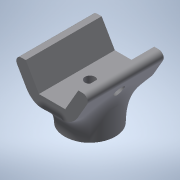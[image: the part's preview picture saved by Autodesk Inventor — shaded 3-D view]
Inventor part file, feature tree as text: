
AUTODESK INVENTOR PART (.ipt)
format: ipt  version: 2020 (Build 240168000, 168)  size: 770,560 bytes
history: native  units: mm
features: other x7, extrude x4, sketch x4, fillet x3, mirror x1, reference x1
ambient origin geometry x8: Origin, YZ Plane, XZ Plane, XY Plane, X Axis, Y Axis, Z Axis, Center Point
bodies: Body1 (feature_tree)
feature tree (20):
  other  "Твердое тело1"
  extrude  "Выдавливание1"  Depth=5.0mm
  other  "Непосредственное редактирование1"
  fillet  "Сопряжение1"  Radius=5.0mm
  extrude  "Выдавливание2"  Depth=5.0mm
  extrude  "Выдавливание3"  Depth=30.0mm TaperAngle=0.0deg
  fillet  "Сопряжение4"  [1 undecoded]
  fillet  "Сопряжение5"  [1 undecoded]
  extrude  "Выдавливание5"  TaperAngle=0.0deg  [1 undecoded]
  mirror  "Зеркальное отражение2"
  sketch  "Эскиз1"
  sketch  "Эскиз2"
  sketch  "Эскиз3"
  sketch  "Эскиз5"
  reference  "Ссылка1"
  other  "Перенос1"
  other  "Перенос2"
  other  "Перенос3"
  other  "КВ33.000.100 - Блок переключение передач.iam"
  other  "КВ33.000.105 - Каретка:2"
note: 3 required parameter values undecoded (feature->parameter linkage not recoverable at this tier; creation-order binding heuristic only, values carry confidence <= 0.55)
